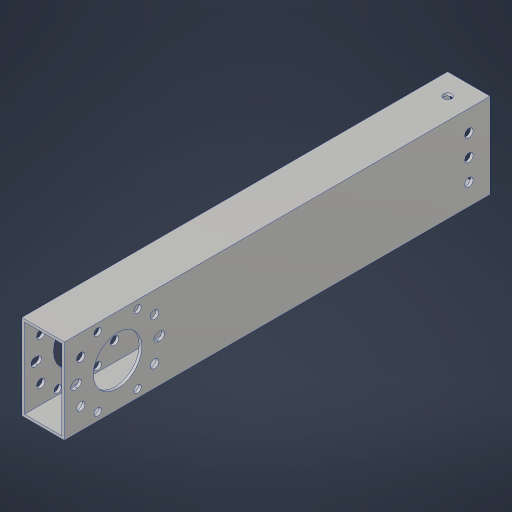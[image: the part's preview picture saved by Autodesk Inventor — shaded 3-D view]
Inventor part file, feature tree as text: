
AUTODESK INVENTOR PART (.ipt)
format: ipt  version: 2023.4 (Build 274418000, 418)  size: 250,880 bytes
history: native  units: in
note: dims shown in document units (in); Inventor stores cm internally (conversion verified against a paired STEP export)
features: hole x5, sketch x4, projected_geometry x3, extrude x2
ambient origin geometry x8: Origin, YZ Plane, XZ Plane, XY Plane, X Axis, Y Axis, Z Axis, Center Point
bodies: Solid1 (feature_tree)
feature tree (14):
  extrude  "Extrusion1"  Depth=1.25in
  sketch  "Sketch2"  dims[d4=0.0in d5=1.25in]
  hole  "Hole1"  [1 undecoded]
  hole  "Hole2"  [1 undecoded]
  hole  "Hole3"  [1 undecoded]
  extrude  "Extrusion2"  Depth=1.0in
  hole  "Hole4"  [1 undecoded]
  hole  "Hole5"  [1 undecoded]
  sketch  "Sketch3"  dims[d6=1.14in d7=0.75in d8=0.375in d9=0.25in d10=0.5635in d11=1.0in d12=0.8108in d13=1.875in]
  sketch  "Sketch4"  dims[d14=2.0in d15=4.7244in d17=360.0deg]
  sketch  "Sketch5"  dims[d19=2.3622in d21=360.0deg d23=0.201in d24=0.75in d25=0.332in d26=0.25in d27=0.5635in d28=1.0in d29=0.8108in d30=0.177in d31=0.75in d32=0.385in d33=0.25in d34=0.5635in d35=1.0in d36=0.8108in d37=0.52in d38=1.5in d39=1.0in d40=0.0in d41=0.5in d42=0.5in d43=0.5in d44=0.201in d45=0.75in d46=0.385in d47=0.25in d48=0.5635in d49=1.0in d50=0.8108in d51=0.5in d52=0.201in d53=0.75in d54=0.375in d55=0.25in d56=0.5635in d57=1.0in d58=0.8108in]
  projected_geometry  "Project Cut Edges1"
  projected_geometry  "Project Cut Edges2"
  projected_geometry  "Project Cut Edges3"
note: 5 required parameter values undecoded (feature->parameter linkage not recoverable at this tier; creation-order binding heuristic only, values carry confidence <= 0.55)
